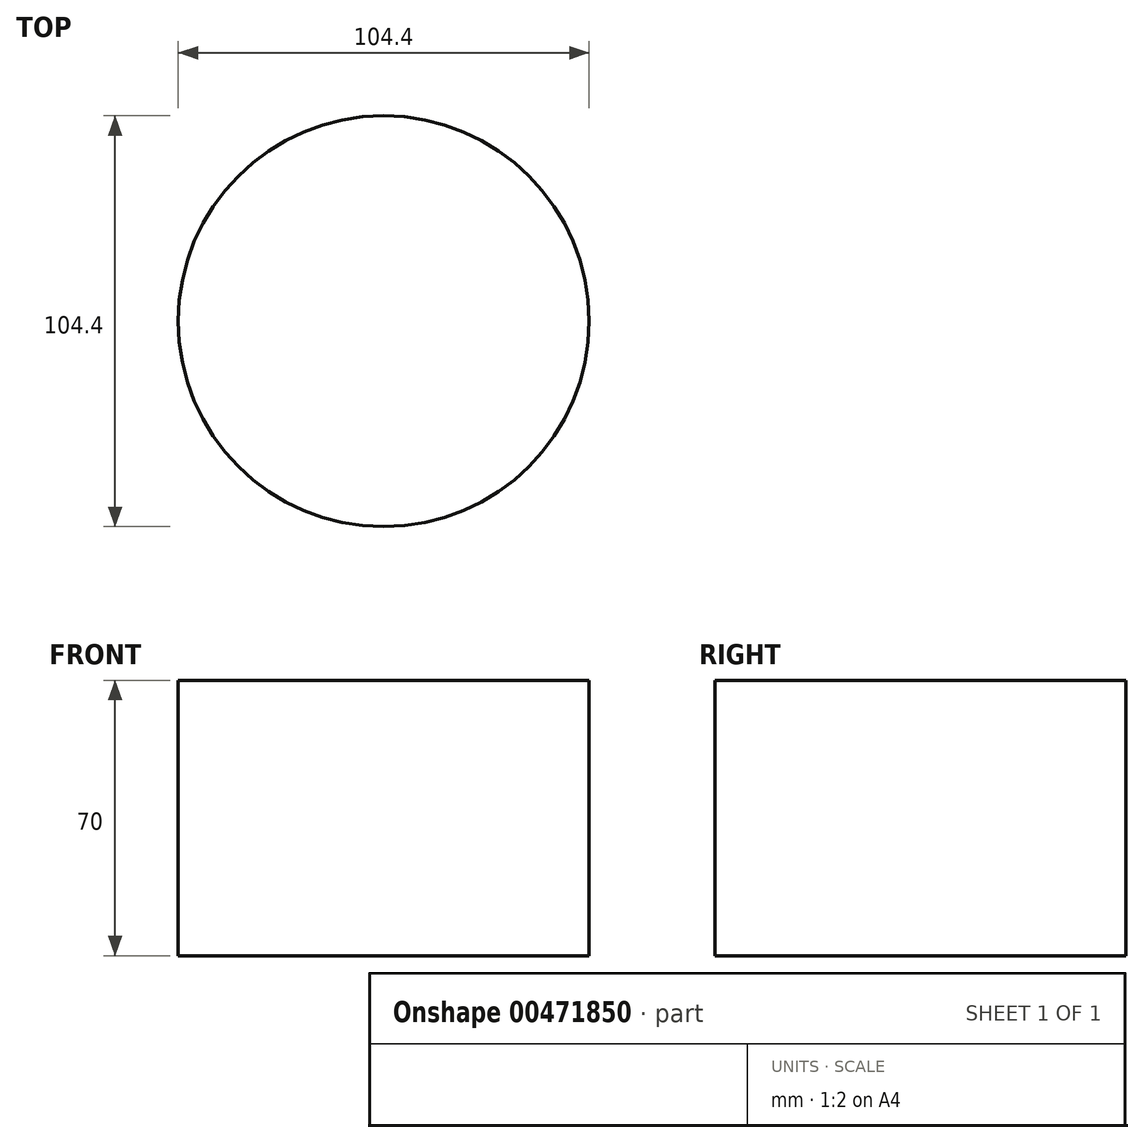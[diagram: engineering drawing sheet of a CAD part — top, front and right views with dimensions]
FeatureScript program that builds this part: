
annotation { "Feature Type Name" : "Feature", "Feature Type Description" : "" }
export const myFeature = defineFeature(function(context is Context, id is Id, definition is map)
    precondition{}
    {
        {
            var Q0;
            Q0=qCreatedBy(makeId("Top.planeOp"),FACE);
            var sketch = newSketch(context, id + "F0", { "sketchPlane" : qUnion([Q0])});
            skCircle(sketch, "E0", {"center": v(0, 0) * mm, "radius": 52.2 * mm});
            skSolve(sketch);
        }
        {
            var Q0;
            Q0=makeQuery(id+"F0.imprint","IMPRINT",FACE,{"disambiguationData":[TD([[makeQuery(id+"F0.imprint","IMPRINT",EDGE,{"derivedFrom":sQuery(id+"F0.wireOp",EDGE,"E0")}),1.0]])]});
            extrude(context, id + "F1", {"entities" : qUnion([Q0]), "depth" : 70 * mm});
        }
    });
